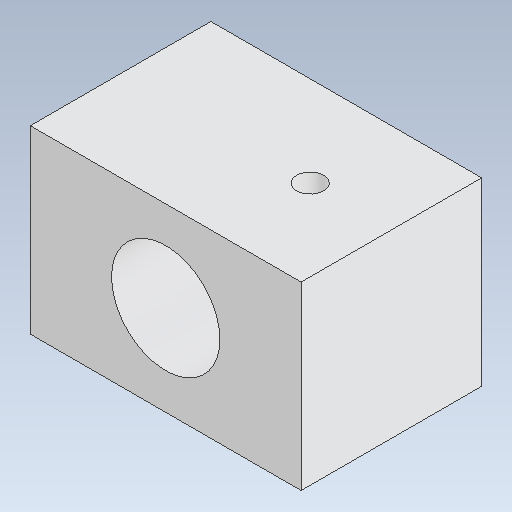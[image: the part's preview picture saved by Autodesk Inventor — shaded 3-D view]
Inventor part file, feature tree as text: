
AUTODESK INVENTOR PART (.ipt)
format: ipt  version: 2020.5 (Build 245400000, 400)  size: 112,640 bytes
history: native  units: mm
features: extrude x3, sketch x3
ambient origin geometry x8: Origin, YZ Plane, XZ Plane, XY Plane, X Axis, Y Axis, Z Axis, Center Point
bodies: Solid1 (feature_tree)
feature tree (6):
  extrude  "Extrusion1"  Depth=20.0mm
  sketch  "Sketch2"  dims[d0=12.0mm d1=20.0mm]
  extrude  "Extrusion2"  Depth=30.0mm
  extrude  "Extrusion3"  Depth=10.0mm
  sketch  "Sketch3"  dims[d2=20.0mm d3=0.0mm d4=30.0mm]
  sketch  "Sketch4"  dims[d5=10.0mm d6=0.0mm d7=3.0mm d8=10.0mm d9=0.0mm]
